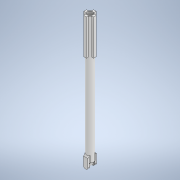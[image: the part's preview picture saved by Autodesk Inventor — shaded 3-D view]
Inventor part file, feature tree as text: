
AUTODESK INVENTOR PART (.ipt)
format: ipt  version: 2022 (Build 260153000, 153)  size: 255,488 bytes
history: native  units: in
note: dims shown in document units (in); Inventor stores cm internally (conversion verified against a paired STEP export)
features: extrude x5, fillet x5, sketch x5
ambient origin geometry x8: Origin, YZ Plane, XZ Plane, XY Plane, X Axis, Y Axis, Z Axis, Center Point
bodies: Body1 (feature_tree)
feature tree (15):
  extrude  "Extrusion7"  Depth=4.6063in TaperAngle=0.0deg
  extrude  "Extrusion8"  Depth=0.1142in
  extrude  "Extrusion9"  Depth=0.1142in
  fillet  "Fillet1"  Radius=0.1142in
  fillet  "Fillet3"  Radius=0.1142in
  fillet  "Fillet5"  Radius=0.1142in
  fillet  "Fillet6"  Radius=0.1142in
  fillet  "Fillet7"  Radius=0.7087in
  extrude  "Extrusion11"  Depth=0.189in
  extrude  "Extrusion12"  Depth=0.0945in
  sketch  "Sketch7"  dims[d71=0.2953in d72=4.6063in d73=0.0in]
  sketch  "Sketch8"  dims[d74=0.1142in d75=0.1142in]
  sketch  "Sketch9"  dims[d76=0.1142in d77=0.1142in d78=0.1142in d79=0.1142in d80=0.1142in d81=0.1142in d82=0.7087in d83=0.0in]
  sketch  "Sketch11"  dims[d84=0.7874in d85=0.0in d86=0.189in]
  sketch  "Sketch12"  dims[d87=0.0728in d88=0.1083in d90=0.0728in d91=0.2165in d93=0.2362in d94=0.1969in d95=0.0in d96=0.0in d97=0.0787in d99=0.0394in d106=0.0394in d107=0.0197in d108=0.0945in d109=0.1181in d110=0.0984in d111=0.0984in d112=0.3937in d113=0.0in d115=0.2362in d116=0.315in d117=0.0in d121=0.0945in d122=0.0945in d123=0.189in d98=0.0in d100=0.0in d101=0.0in d118=0.0197in d119=0.0344in d120=0.0197in]
